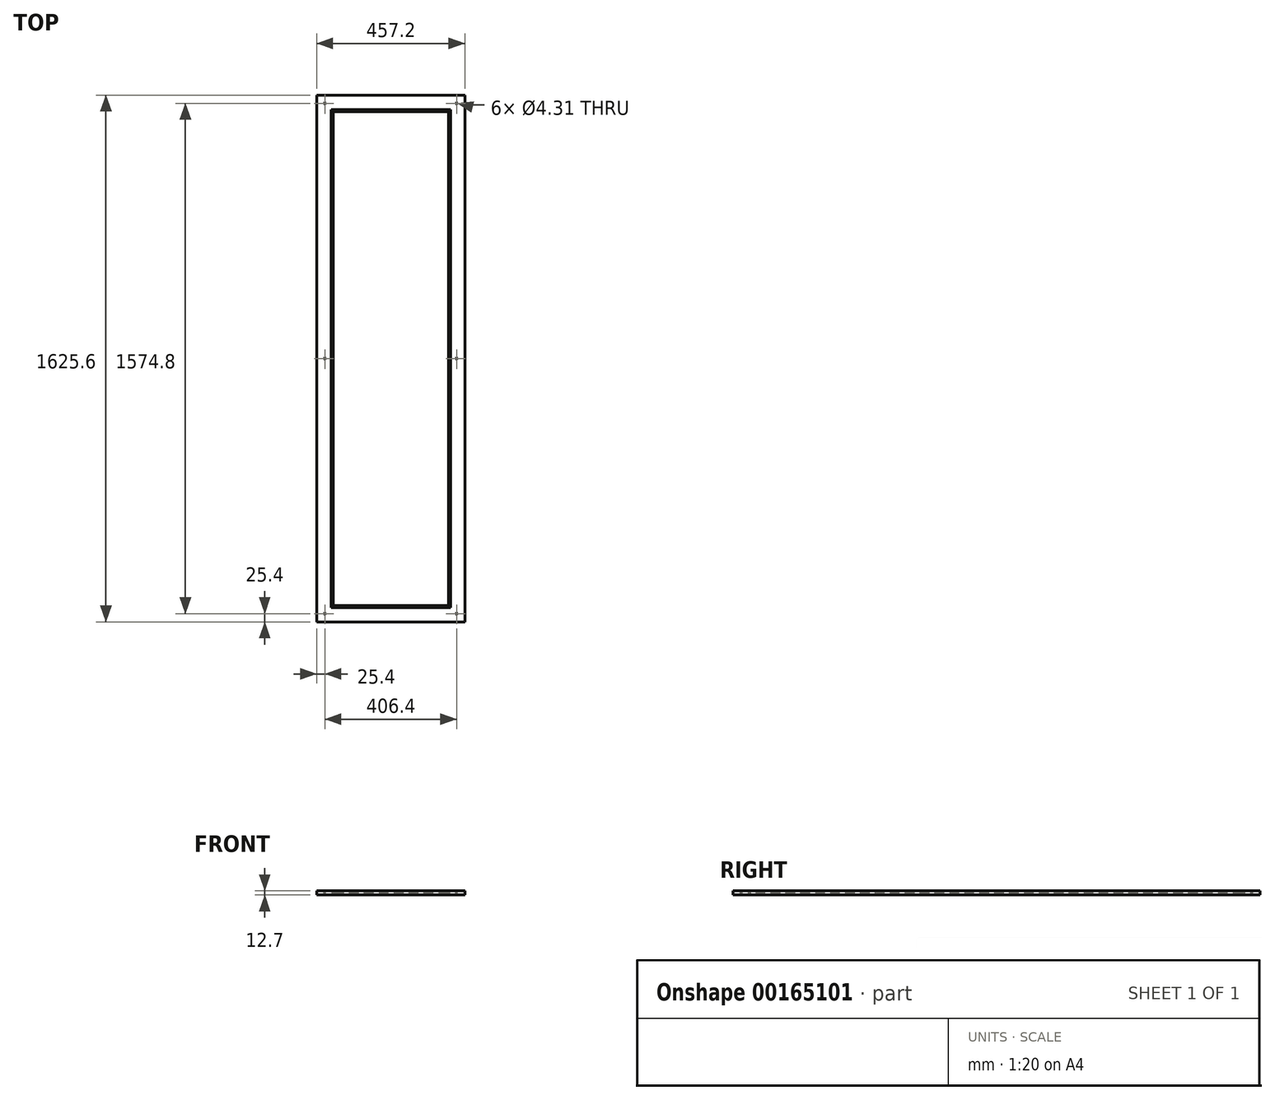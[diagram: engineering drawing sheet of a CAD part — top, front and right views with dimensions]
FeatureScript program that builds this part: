
annotation { "Feature Type Name" : "Feature", "Feature Type Description" : "" }
export const myFeature = defineFeature(function(context is Context, id is Id, definition is map)
    precondition{}
    {
        {
            var Q0;
            Q0=qCreatedBy(makeId("Top.planeOp"),FACE);
            var sketch = newSketch(context, id + "F0", { "sketchPlane" : qUnion([Q0])});
            skLineSegment(sketch, "E0.bottom", {"start": v(-177.8, -762) * mm, "end": v(177.8, -762) * mm});
            skLineSegment(sketch, "E0.top", {"start": v(-177.8, 762) * mm, "end": v(177.8, 762) * mm});
            skLineSegment(sketch, "E0.left", {"start": v(-177.8, -762) * mm, "end": v(-177.8, 762) * mm});
            skLineSegment(sketch, "E0.right", {"start": v(177.8, -762) * mm, "end": v(177.8, 762) * mm});
            skPoint(sketch, "E0.middle", {"position": v(0, 0) * mm});
            skLineSegment(sketch, "E1.bottom", {"start": v(228.6, -812.8) * mm, "end": v(-228.6, -812.8) * mm});
            skLineSegment(sketch, "E1.top", {"start": v(228.6, 812.8) * mm, "end": v(-228.6, 812.8) * mm});
            skLineSegment(sketch, "E1.left", {"start": v(228.6, -812.8) * mm, "end": v(228.6, 812.8) * mm});
            skLineSegment(sketch, "E1.right", {"start": v(-228.6, -812.8) * mm, "end": v(-228.6, 812.8) * mm});
            skLineSegment(sketch, "E2", {"start": v(177.8, -762) * mm, "end": v(177.8, -812.8) * mm, "construction": true});
            skLineSegment(sketch, "E3", {"start": v(177.8, -762) * mm, "end": v(228.6, -762) * mm, "construction": true});
            skSolve(sketch);
        }
        {
            var Q0;
            Q0 = qSketchRegion(id + "F0", true);
            extrude(context, id + "F1", {"entities" : qUnion([Q0]), "depth" : 12.7 * mm});
        }
        {
            var Q0;
            Q0=makeQuery(id+"F1.opExtrude","CAP_EDGE",EDGE,{"disambiguationData":[OSD([sQuery(id+"F0.wireOp",EDGE,"E0.top")])],"isStart":false});
            var Q1;
            Q1=makeQuery(id+"F1.opExtrude","CAP_EDGE",EDGE,{"disambiguationData":[OSD([sQuery(id+"F0.wireOp",EDGE,"E0.left")])],"isStart":false});
            var Q2;
            Q2=makeQuery(id+"F1.opExtrude","CAP_EDGE",EDGE,{"disambiguationData":[OSD([sQuery(id+"F0.wireOp",EDGE,"E0.right")])],"isStart":false});
            var Q3;
            Q3=makeQuery(id+"F1.opExtrude","CAP_EDGE",EDGE,{"disambiguationData":[OSD([sQuery(id+"F0.wireOp",EDGE,"E0.bottom")])],"isStart":false});
            chamfer(context, id + "F2", {"entities" : qUnion([Q0, Q1, Q2, Q3]), "width" : 6.35 * mm, "tangentPropagation" : true});
        }
        {
            var Q0;
            Q0=makeQuery(id+"F1.opExtrude","CAP_FACE",FACE,{"disambiguationData":[OSD([sQuery(id+"F0.wireOp",EDGE,"E0.bottom"),sQuery(id+"F0.wireOp",EDGE,"E0.top"),sQuery(id+"F0.wireOp",EDGE,"E0.left"),sQuery(id+"F0.wireOp",EDGE,"E0.right"),sQuery(id+"F0.wireOp",EDGE,"E1.bottom"),sQuery(id+"F0.wireOp",EDGE,"E1.top"),sQuery(id+"F0.wireOp",EDGE,"E1.left"),sQuery(id+"F0.wireOp",EDGE,"E1.right")])],"isStart":true});
            var sketch = newSketch(context, id + "F3", { "sketchPlane" : qUnion([Q0])});
            skCircle(sketch, "E4", {"center": v(-177.8, -762) * mm, "radius": 3.17 * mm});
            skCircle(sketch, "E5", {"center": v(177.8, -762) * mm, "radius": 3.17 * mm});
            skCircle(sketch, "E6", {"center": v(177.8, 762) * mm, "radius": 3.17 * mm});
            skCircle(sketch, "E7", {"center": v(-177.8, 762) * mm, "radius": 3.17 * mm});
            skSolve(sketch);
        }
        {
            var Q0;
            Q0 = qSketchRegion(id + "F3", true);
            var Q1;
            Q1=makeQuery(id+"F1.opExtrude","CAP_FACE",FACE,{"disambiguationData":[OSD([sQuery(id+"F0.wireOp",EDGE,"E0.bottom"),sQuery(id+"F0.wireOp",EDGE,"E0.top"),sQuery(id+"F0.wireOp",EDGE,"E0.left"),sQuery(id+"F0.wireOp",EDGE,"E0.right"),sQuery(id+"F0.wireOp",EDGE,"E1.bottom"),sQuery(id+"F0.wireOp",EDGE,"E1.top"),sQuery(id+"F0.wireOp",EDGE,"E1.left"),sQuery(id+"F0.wireOp",EDGE,"E1.right")])],"isStart":false});
            extrude(context, id + "F4", {"entities" : qUnion([Q0]), "operationType" : NewBodyOperationType.REMOVE, "endBound" : BoundingType.UP_TO_SURFACE, "oppositeDirection" : true, "endBoundEntityFace" : qUnion([Q1]), "depth" : 25.4 * mm});
        }
        {
            var Q0;
            Q0=makeQuery(id+"F1.opExtrude","CAP_FACE",FACE,{"disambiguationData":[OSD([sQuery(id+"F0.wireOp",EDGE,"E0.bottom"),sQuery(id+"F0.wireOp",EDGE,"E0.top"),sQuery(id+"F0.wireOp",EDGE,"E0.left"),sQuery(id+"F0.wireOp",EDGE,"E0.right"),sQuery(id+"F0.wireOp",EDGE,"E1.bottom"),sQuery(id+"F0.wireOp",EDGE,"E1.top"),sQuery(id+"F0.wireOp",EDGE,"E1.left"),sQuery(id+"F0.wireOp",EDGE,"E1.right")])],"isStart":false});
            var sketch = newSketch(context, id + "F5", { "sketchPlane" : qUnion([Q0])});
            skLineSegment(sketch, "E8.bottom", {"start": v(-203.2, -787.4) * mm, "end": v(203.2, -787.4) * mm, "construction": true});
            skLineSegment(sketch, "E8.top", {"start": v(-203.2, 787.4) * mm, "end": v(203.2, 787.4) * mm, "construction": true});
            skLineSegment(sketch, "E8.left", {"start": v(-203.2, -787.4) * mm, "end": v(-203.2, 787.4) * mm, "construction": true});
            skLineSegment(sketch, "E8.right", {"start": v(203.2, -787.4) * mm, "end": v(203.2, 787.4) * mm, "construction": true});
            skPoint(sketch, "E8.middle", {"position": v(0, 0) * mm});
            skLineSegment(sketch, "E9.bottom", {"start": v(-203.2, -787.4) * mm, "end": v(-228.6, -787.4) * mm, "construction": true});
            skLineSegment(sketch, "E9.top", {"start": v(-203.2, -812.8) * mm, "end": v(-228.6, -812.8) * mm, "construction": true});
            skLineSegment(sketch, "E9.left", {"start": v(-203.2, -787.4) * mm, "end": v(-203.2, -812.8) * mm, "construction": true});
            skLineSegment(sketch, "E9.right", {"start": v(-228.6, -787.4) * mm, "end": v(-228.6, -812.8) * mm, "construction": true});
            skCircle(sketch, "E10", {"center": v(-203.2, -787.4) * mm, "radius": 2.15 * mm});
            skCircle(sketch, "E11", {"center": v(203.2, -787.4) * mm, "radius": 2.15 * mm});
            skCircle(sketch, "E12", {"center": v(203.2, 0) * mm, "radius": 2.15 * mm});
            skCircle(sketch, "E13", {"center": v(-203.2, 0) * mm, "radius": 2.15 * mm});
            skCircle(sketch, "E14", {"center": v(-203.2, 787.4) * mm, "radius": 2.15 * mm});
            skCircle(sketch, "E15", {"center": v(203.2, 787.4) * mm, "radius": 2.15 * mm});
            skSolve(sketch);
        }
        {
            var Q0;
            Q0 = qSketchRegion(id + "F5", true);
            var Q1;
            Q1=makeQuery(id+"F1.opExtrude","CAP_FACE",FACE,{"disambiguationData":[OSD([sQuery(id+"F0.wireOp",EDGE,"E0.bottom"),sQuery(id+"F0.wireOp",EDGE,"E0.top"),sQuery(id+"F0.wireOp",EDGE,"E0.left"),sQuery(id+"F0.wireOp",EDGE,"E0.right"),sQuery(id+"F0.wireOp",EDGE,"E1.bottom"),sQuery(id+"F0.wireOp",EDGE,"E1.top"),sQuery(id+"F0.wireOp",EDGE,"E1.left"),sQuery(id+"F0.wireOp",EDGE,"E1.right")])],"isStart":true});
            extrude(context, id + "F6", {"entities" : qUnion([Q0]), "operationType" : NewBodyOperationType.REMOVE, "endBound" : BoundingType.UP_TO_SURFACE, "oppositeDirection" : true, "endBoundEntityFace" : qUnion([Q1]), "depth" : 25.4 * mm});
        }
    });
